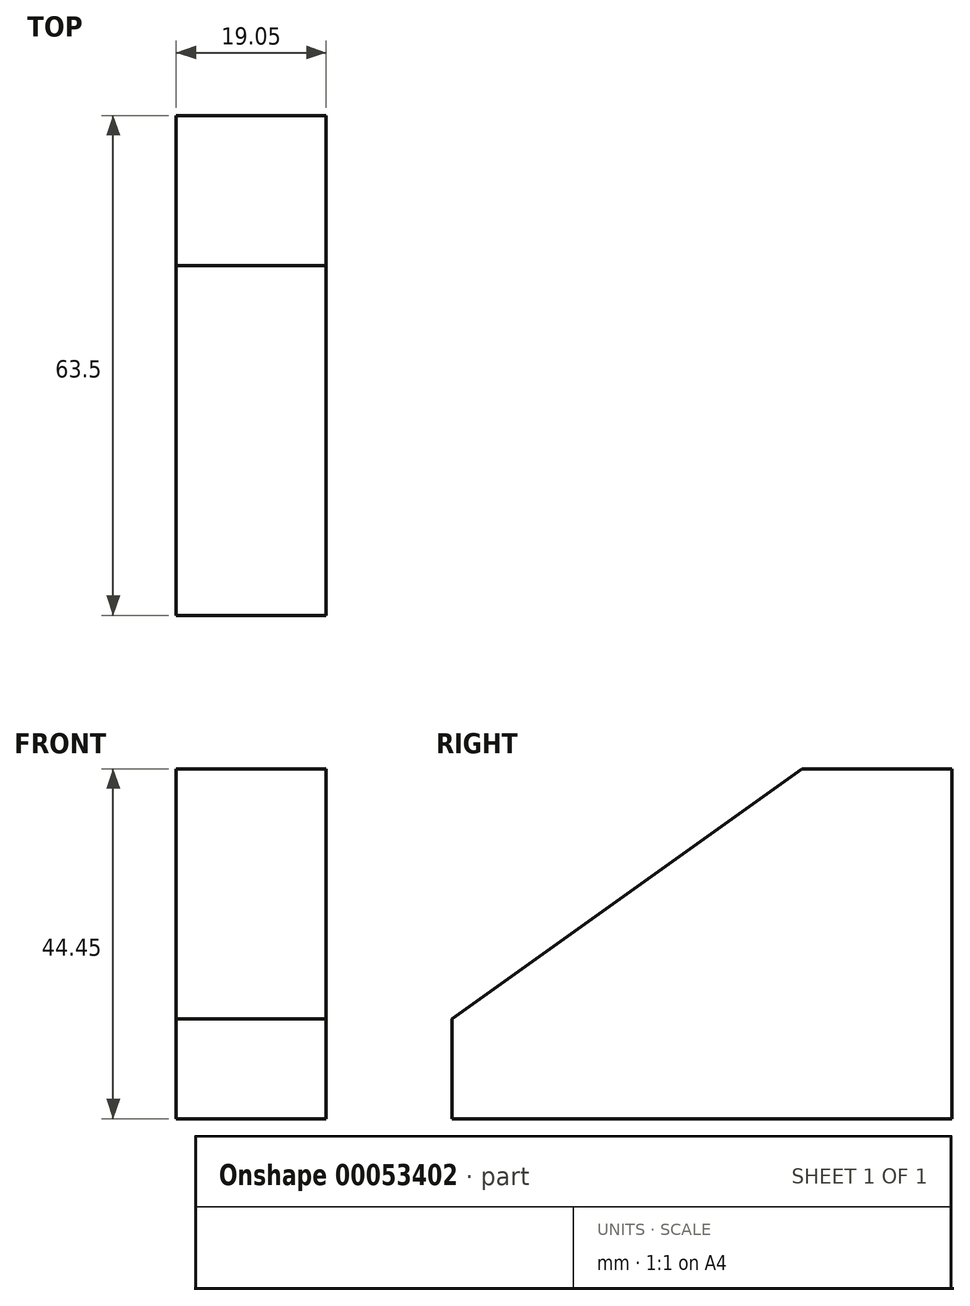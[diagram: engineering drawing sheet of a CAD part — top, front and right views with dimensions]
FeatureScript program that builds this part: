
annotation { "Feature Type Name" : "Feature", "Feature Type Description" : "" }
export const myFeature = defineFeature(function(context is Context, id is Id, definition is map)
    precondition{}
    {
        {
            var Q0;
            Q0=qCreatedBy(makeId("Right.planeOp"),FACE);
            var sketch = newSketch(context, id + "F0", { "sketchPlane" : qUnion([Q0])});
            skLineSegment(sketch, "E0", {"start": v(-31.24, -18.46) * mm, "end": v(32.26, -18.46) * mm});
            skLineSegment(sketch, "E1", {"start": v(32.26, -18.46) * mm, "end": v(32.26, 25.99) * mm});
            skLineSegment(sketch, "E2", {"start": v(-31.24, -18.46) * mm, "end": v(-31.24, -5.76) * mm});
            skLineSegment(sketch, "E3", {"start": v(32.26, 25.99) * mm, "end": v(13.21, 25.99) * mm});
            skLineSegment(sketch, "E4", {"start": v(13.21, 25.99) * mm, "end": v(-31.24, -5.76) * mm});
            skSolve(sketch);
        }
        {
            var Q0;
            Q0 = qSketchRegion(id + "F0", true);
            extrude(context, id + "F1", {"entities" : qUnion([Q0]), "depth" : 19.05 * mm});
        }
    });
